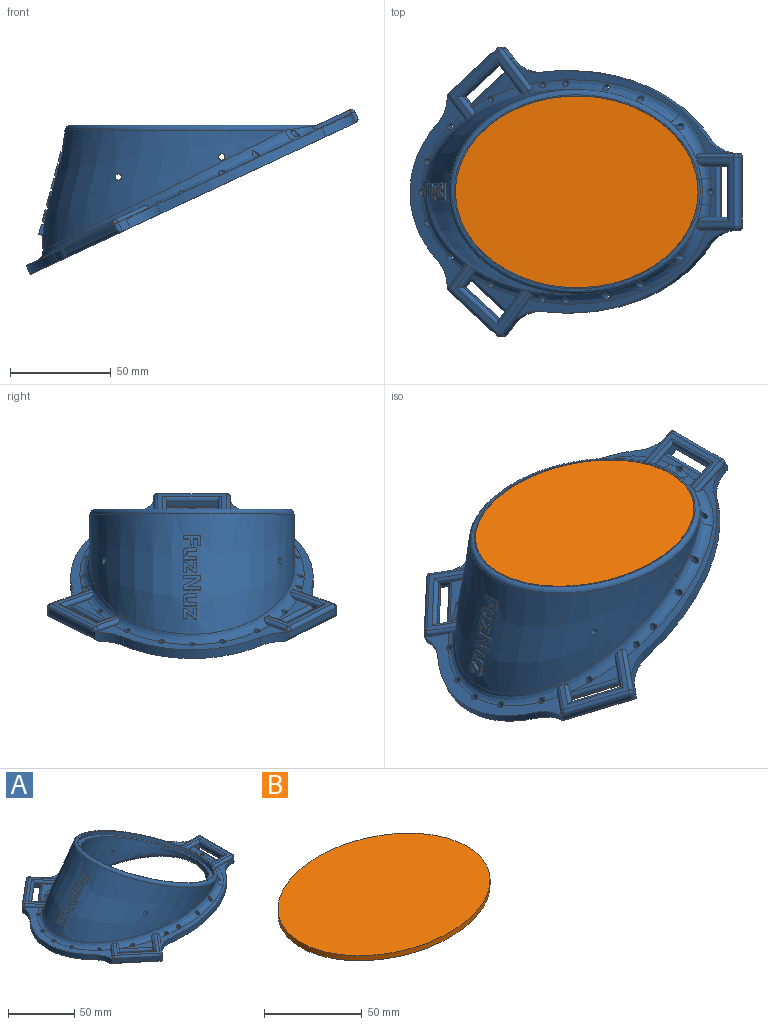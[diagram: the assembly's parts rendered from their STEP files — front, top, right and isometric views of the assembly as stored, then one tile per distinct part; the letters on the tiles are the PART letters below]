
ASSEMBLY  parts=2 mates=1
PART A: 209 faces, bbox 180.8x145.5x60.1 mm
  f0: bspline ~145.19x101.6mm, area 9514.1mm2, adj f10,f18,f19,f20,f21,f22,f125,f126
  f1: plane 24.98x16.69mm, normal (0,0,1), area 97.4mm2, adj f10,f36,f59,f60,f97
  f2: plane 13.2x11.08mm, normal (-0.77,-0.64,0), area 19.5mm2, adj f10,f11,f49,f87,f98,f100,f124
  f3: plane 178.75x142.51mm, normal (0,0,-1), area 5639.8mm2, adj f6,f8,f16,f24,f26,f27,f29,f30
  f4: bspline ~140.7x88.9mm, area 10555.1mm2, adj f18,f19,f20,f21,f67,f68
  f5: plane 25.41x3.72mm, normal (0,0,1), area 69.3mm2, adj f12,f13,f14,f27,f52,f53,f70
  f6: extruded ~90.53x33.28mm, area 480mm2, adj f3,f7,f85,f90
  f7: plane 122.83x47.16mm, normal (0,0,1), area 433.4mm2, adj f6,f10,f12,f35,f54,f62,f85,f90
  f8: extruded ~68.2x15.01mm, area 365mm2, adj f3,f9,f89,f92
  f9: plane 98.89x28.6mm, normal (0,0,1), area 617.6mm2, adj f8,f10,f24,f30,f31,f32,f37,f48
  f10: bspline ~145.09x111.78mm, area 2304.7mm2, adj f0,f1,f2,f7,f9,f11,f12,f14
  f11: plane 24.97x16.69mm, normal (0,0,1), area 97.4mm2, adj f2,f10,f33,f46,f98
  f12: bspline ~38.11x22.09mm, area 191.3mm2, adj f5,f7,f10,f13,f22,f28,f29,f51
  f13: bspline ~21.06x5.16mm, area 55.7mm2, adj f5,f12,f14,f23,f27
  f14: bspline ~37.9x21.75mm, area 191.3mm2, adj f5,f10,f13,f17,f22,f25,f26,f51
  f15: plane 110.97x96.55mm, normal (0.42,0,0.91), area 228.7mm2, adj f22,f23,f69
  f16: extruded ~90.53x33.28mm, area 480mm2, adj f3,f17,f86,f91
  f17: plane 122.83x47.16mm, normal (0,0,1), area 433.4mm2, adj f10,f14,f16,f34,f47,f55,f86,f91
  f18: cylinder r=1.59mm len=6.47mm, axis (0,-1,0), area 64.6mm2, adj f0,f4
  f19: cylinder r=1.59mm len=6.47mm, axis (0,-1,0), area 64.6mm2, adj f0,f4
  f20: cylinder r=1.59mm len=6.87mm, axis (0,-1,0), area 68.6mm2, adj f0,f4
  f21: cylinder r=1.59mm len=6.87mm, axis (0,-1,0), area 68.6mm2, adj f0,f4
  f22: bspline ~115.08x101.58mm, area 1264.8mm2, adj f0,f12,f14,f15,f23
  f23: bspline ~19.62x2.95mm, area 14.2mm2, adj f13,f15,f22
  f24: cylinder r=1.59mm len=4.78mm, axis (0,0,-1), area 47.6mm2, adj f3,f9,f10
  f25: cone r=0mm half-angle=59deg, axis (0,0,-1), area 1.7mm2, adj f14,f26
  f26: cylinder r=1.59mm len=9.53mm, axis (0,0,-1), area 74.5mm2, adj f3,f14,f25
  f27: cylinder r=1.59mm len=5.05mm, axis (0,0,-1), area 48.3mm2, adj f3,f5,f13
  f28: cone r=0mm half-angle=59deg, axis (0,0,-1), area 1.7mm2, adj f12,f29
  f29: cylinder r=1.59mm len=9.53mm, axis (0,0,-1), area 74.5mm2, adj f3,f12,f28
  f30: cylinder r=1.59mm len=4.78mm, axis (0,0,-1), area 47.6mm2, adj f3,f9,f10
  f31: cylinder r=1.59mm len=4.78mm, axis (0,0,-1), area 47.6mm2, adj f3,f9,f10
  f32: cylinder r=1.59mm len=5.31mm, axis (0,0,-1), area 49.2mm2, adj f3,f9,f10
  f33: cylinder r=1.59mm len=5.53mm, axis (0,0,-1), area 50.1mm2, adj f3,f10,f11
  f34: cylinder r=1.59mm len=5.89mm, axis (0,0,-1), area 51.7mm2, adj f3,f10,f17
  f35: cylinder r=1.59mm len=5.89mm, axis (0,0,-1), area 51.7mm2, adj f3,f7,f10
  f36: cylinder r=1.59mm len=5.53mm, axis (0,0,-1), area 50.1mm2, adj f1,f3,f10
  f37: cylinder r=1.59mm len=5.31mm, axis (0,0,-1), area 49.2mm2, adj f3,f9,f10
  f38: cylinder r=1.59mm len=5.11mm, axis (0,0,-1), area 51mm2, adj f3,f10
  f39: cylinder r=1.59mm len=5.61mm, axis (0,0,-1), area 56mm2, adj f3,f10
  f40: cylinder r=1.59mm len=8.91mm, axis (0,0,-1), area 64.6mm2, adj f3,f10
  f41: cylinder r=1.59mm len=8.91mm, axis (0,0,-1), area 64.6mm2, adj f3,f10
  f42: cylinder r=1.59mm len=5.61mm, axis (0,0,-1), area 56mm2, adj f3,f10
  f43: cylinder r=1.59mm len=5.11mm, axis (0,0,-1), area 51mm2, adj f3,f10
  f44: plane 43.13x33.71mm, normal (0,0,1), area 179.1mm2, adj f10,f45,f114,f117,f118,f122,f123,f124
  f45: plane 2.15x1.82mm, normal (0.64,-0.77,0), area 1.3mm2, adj f10,f44,f117
  f46: plane 6.87x5.77mm, normal (0.77,0.64,0), area 17mm2, adj f10,f11,f49,f87,f98,f101,f122
  f47: plane 19.16x16.08mm, normal (0.77,0.64,0), area 38.9mm2, adj f3,f10,f17,f91,f117,f121
  f48: plane 9.68x8.13mm, normal (-0.77,-0.64,0), area 3.7mm2, adj f9,f10,f114,f115
  f49: plane 19.46x16.33mm, normal (0.64,-0.77,0), area 80.6mm2, adj f2,f46,f99,f123
  f50: plane 27.73x23.27mm, normal (-0.64,0.77,0), area 114.3mm2, adj f9,f92,f115,f118,f120,f121
  f51: plane 34.3x20.36mm, normal (0,0,1), area 175.5mm2, adj f12,f14,f74,f76,f77,f82,f83,f84
  f52: plane 14.1x5.12mm, normal (0,-1,0), area 28.7mm2, adj f3,f5,f14,f56,f66,f70,f71,f73
  f53: plane 12.19x3.21mm, normal (0,1,0), area 18mm2, adj f5,f12,f56,f66,f70,f72,f84
  f54: plane 18.45x5.13mm, normal (0,-1,0), area 9.6mm2, adj f3,f7,f12,f76,f81,f85
  f55: plane 18.44x5.12mm, normal (0,1,0), area 9.6mm2, adj f3,f14,f17,f74,f78,f86
  f56: plane 25.4x3.18mm, normal (-1,0,0), area 80.6mm2, adj f52,f53,f71,f83
  f57: plane 34.29x3.18mm, normal (1,0,0), area 108.9mm2, adj f77,f78,f80,f81
  f58: plane 43.13x33.71mm, normal (0,0,1), area 179.1mm2, adj f10,f63,f104,f107,f108,f111,f112,f113
  f59: plane 13.2x11.09mm, normal (-0.77,0.64,0), area 19.5mm2, adj f1,f10,f64,f88,f94,f97,f111
  f60: plane 6.87x5.77mm, normal (0.77,-0.64,0), area 17mm2, adj f1,f10,f64,f88,f95,f97,f113
  f61: plane 9.68x8.13mm, normal (-0.77,0.64,0), area 3.7mm2, adj f9,f10,f107,f110
  f62: plane 19.16x16.08mm, normal (0.77,-0.64,0), area 38.9mm2, adj f3,f7,f10,f90,f104,f105
  f63: plane 2.15x1.82mm, normal (0.64,0.77,0), area 1.3mm2, adj f10,f58,f104
  f64: plane 19.46x16.33mm, normal (0.64,0.77,0), area 80.6mm2, adj f59,f60,f93,f112
  f65: plane 27.73x23.27mm, normal (-0.64,-0.77,0), area 114.3mm2, adj f9,f89,f103,f105,f108,f110
  f66: plane 25.4x0.97mm, normal (1,0,0), area 24.5mm2, adj f52,f53,f70,f73
  f67: bspline ~145.83x95.27mm, area 1856.2mm2, adj f3,f4
  f68: plane 109.35x95.25mm, normal (0.42,0,0.91), area 1021.6mm2, adj f4,f69
  f69: extruded ~110.69x95.25mm, area 1080.5mm2, adj f15,f68
  f70: cylinder r=1.91mm len=25.4mm, axis (0,1,0), area 76mm2, adj f5,f52,f53,f66
  f71: cylinder r=1.91mm len=27.31mm, axis (0,-1,0), area 78.9mm2, adj f3,f52,f56,f72
  f72: cylinder r=1.91mm len=8.59mm, axis (-1,0,0), area 20mm2, adj f3,f53,f71,f73
  f73: cylinder r=1.91mm len=27.31mm, axis (0,1,0), area 78.9mm2, adj f3,f52,f66,f72
  f74: cylinder r=1.91mm len=20.34mm, axis (1,0,0), area 58mm2, adj f14,f51,f55,f75
  f75: sphere r=1.91mm, area 3.6mm2, adj f74,f77,f78
  f76: cylinder r=1.91mm len=20.34mm, axis (-1,0,0), area 58mm2, adj f12,f51,f54,f79
  f77: cylinder r=1.91mm len=34.29mm, axis (0,-1,0), area 102.6mm2, adj f51,f57,f75,f79
  f78: cylinder r=1.91mm len=5.08mm, axis (0,0,-1), area 12.4mm2, adj f55,f57,f75,f80
  f79: sphere r=1.91mm, area 3.6mm2, adj f76,f77,f81
  f80: cylinder r=1.91mm len=38.1mm, axis (0,1,0), area 108.3mm2, adj f3,f57,f78,f81
  f81: cylinder r=1.91mm len=5.08mm, axis (0,0,-1), area 12.4mm2, adj f54,f57,f79,f80
  f82: cylinder r=1.91mm len=17.05mm, axis (-1,0,0), area 43.7mm2, adj f14,f51,f52,f83
  f83: cylinder r=1.91mm len=29.21mm, axis (0,1,0), area 81.7mm2, adj f51,f56,f82,f84
  f84: cylinder r=1.91mm len=17.05mm, axis (1,0,0), area 43.7mm2, adj f12,f51,f53,f83
  f85: cylinder r=19.05mm len=15.51mm, axis (0,0,-1), area 86.6mm2, adj f3,f6,f7,f54
  f86: cylinder r=19.05mm len=15.51mm, axis (0,0,-1), area 86.6mm2, adj f3,f16,f17,f55
  f87: plane 19.46x16.33mm, normal (-0.64,0.77,0), area 24.5mm2, adj f2,f46,f98,f102
  f88: plane 19.46x16.33mm, normal (-0.64,-0.77,0), area 24.5mm2, adj f59,f60,f96,f97
  f89: cylinder r=19.05mm len=14.12mm, axis (0,0,-1), area 71.8mm2, adj f3,f8,f9,f65,f103
  f90: cylinder r=19.05mm len=16.78mm, axis (0,0,-1), area 89.9mm2, adj f3,f6,f7,f62
  f91: cylinder r=19.05mm len=16.78mm, axis (0,0,-1), area 89.9mm2, adj f3,f16,f17,f47
  f92: cylinder r=19.05mm len=14.12mm, axis (0,0,-1), area 71.8mm2, adj f3,f8,f9,f50,f120
  f93: cylinder r=1.91mm len=23.6mm, axis (-0.77,0.64,0), area 81.7mm2, adj f3,f64,f94,f95
  f94: cylinder r=1.91mm len=7.8mm, axis (-0.64,-0.77,0), area 20mm2, adj f3,f59,f93,f96
  f95: cylinder r=1.91mm len=7.8mm, axis (0.64,0.77,0), area 20mm2, adj f3,f60,f93,f96
  f96: cylinder r=1.91mm len=23.6mm, axis (0.77,-0.64,0), area 81.7mm2, adj f3,f88,f94,f95
  f97: cylinder r=1.91mm len=20.68mm, axis (-0.77,0.64,0), area 76mm2, adj f1,f59,f60,f88
  f98: cylinder r=1.91mm len=20.68mm, axis (-0.77,-0.64,0), area 76mm2, adj f2,f11,f46,f87
  f99: cylinder r=1.91mm len=23.6mm, axis (0.77,0.64,0), area 81.7mm2, adj f3,f49,f100,f101
  f100: cylinder r=1.91mm len=7.8mm, axis (0.64,-0.77,0), area 20mm2, adj f2,f3,f99,f102
  f101: cylinder r=1.91mm len=7.8mm, axis (-0.64,0.77,0), area 20mm2, adj f3,f46,f99,f102
  f102: cylinder r=1.91mm len=23.6mm, axis (-0.77,-0.64,0), area 81.7mm2, adj f3,f87,f100,f101
  f103: cylinder r=1.91mm len=31.69mm, axis (0.77,-0.64,0), area 113.7mm2, adj f3,f65,f89,f105
  f104: cylinder r=1.91mm len=21.32mm, axis (-0.64,-0.77,0), area 78.1mm2, adj f10,f58,f62,f63,f106
  f105: cylinder r=1.91mm len=5.08mm, axis (0,0,1), area 12.4mm2, adj f62,f65,f103,f106
  f106: sphere r=1.91mm, area 5.7mm2, adj f104,f105,f108
  f107: cylinder r=1.91mm len=12.89mm, axis (0.64,0.77,0), area 41.6mm2, adj f10,f58,f61,f109
  f108: cylinder r=1.91mm len=27.49mm, axis (-0.77,0.64,0), area 102.6mm2, adj f58,f65,f106,f109
  f109: sphere r=1.91mm, area 8.1mm2, adj f107,f108,f110
  f110: cylinder r=1.91mm len=2.68mm, axis (0,0,-1), area 0.9mm2, adj f9,f61,f65,f109
  f111: cylinder r=1.91mm len=18.68mm, axis (0.64,0.77,0), area 59.8mm2, adj f10,f58,f59,f112
  f112: cylinder r=1.91mm len=23.6mm, axis (0.77,-0.64,0), area 81.7mm2, adj f58,f64,f111,f113
  f113: cylinder r=1.91mm len=11.19mm, axis (-0.64,-0.77,0), area 32.8mm2, adj f10,f58,f60,f112
  f114: cylinder r=1.91mm len=12.89mm, axis (-0.64,0.77,0), area 41.6mm2, adj f10,f44,f48,f116
  f115: cylinder r=1.91mm len=2.68mm, axis (0,0,-1), area 0.9mm2, adj f9,f48,f50,f116
  f116: sphere r=1.91mm, area 5.7mm2, adj f114,f115,f118
  f117: cylinder r=1.91mm len=21.32mm, axis (0.64,-0.77,0), area 78.1mm2, adj f10,f44,f45,f47,f119
  f118: cylinder r=1.91mm len=27.49mm, axis (0.77,0.64,0), area 102.6mm2, adj f44,f50,f116,f119
  f119: sphere r=1.91mm, area 7.8mm2, adj f117,f118,f121
  f120: cylinder r=1.91mm len=31.69mm, axis (-0.77,-0.64,0), area 113.7mm2, adj f3,f50,f92,f121
  f121: cylinder r=1.91mm len=5.08mm, axis (0,0,1), area 12.4mm2, adj f47,f50,f119,f120
  f122: cylinder r=1.91mm len=11.19mm, axis (0.64,-0.77,0), area 32.8mm2, adj f10,f44,f46,f123
  f123: cylinder r=1.91mm len=23.6mm, axis (-0.77,-0.64,0), area 81.7mm2, adj f44,f49,f122,f124
  f124: cylinder r=1.91mm len=18.68mm, axis (-0.64,0.77,0), area 59.8mm2, adj f2,f10,f44,f123
  f125: plane 1.99x1.81mm, normal (0,1,0), area 1.6mm2, adj f0,f126,f132,f134
  f126: plane 8.61x0.65mm, normal (0.64,0,0.77), area 6mm2, adj f0,f125,f127,f132
  f127: plane 4.49x3.84mm, normal (0,-1,0), area 4.8mm2, adj f0,f126,f128,f132
  f128: plane 1.5x0.82mm, normal (-0.64,0,-0.77), area 1.5mm2, adj f0,f127,f129,f132
  f129: plane 3.02x2.66mm, normal (0,1,0), area 2.8mm2, adj f0,f128,f130,f132
  f130: plane 2.23x0.64mm, normal (-0.64,0,-0.77), area 1.7mm2, adj f0,f129,f131,f132
  f131: plane 2.79x2.45mm, normal (0,-1,0), area 2.3mm2, adj f0,f130,f132,f133
  f132: plane 8.61x3.78mm, normal (-0.77,0,0.64), area 24.5mm2, adj f125,f126,f127,f128,f129,f130,f131,f133
  f133: plane 1.5x0.66mm, normal (-0.64,0,-0.77), area 1.3mm2, adj f0,f131,f132,f135
  f134: plane 3.43x0.76mm, normal (-0.64,0,-0.77), area 2.8mm2, adj f0,f125,f132,f135
  f135: plane 2.79x2.45mm, normal (0,1,0), area 2.3mm2, adj f0,f132,f133,f134
  f136: plane 0.97x0.92mm, normal (0.62,0.28,0.74), area 1mm2, adj f0,f137,f150,f152
  f137: plane 0.88x0.76mm, normal (0,1,0), area 0.1mm2, adj f0,f136,f138,f150
  f138: extruded ~1.39x1.35mm, area 1.2mm2, adj f0,f137,f139,f150
  f139: extruded ~1.66x1.66mm, area 1.4mm2, adj f0,f138,f140,f150
  f140: extruded ~2.08x2mm, area 2.1mm2, adj f0,f139,f141,f150
  f141: extruded ~1.79x1.2mm, area 1.9mm2, adj f0,f140,f142,f150
  f142: plane 4.29x0.72mm, normal (0.64,0,0.77), area 3.9mm2, adj f0,f141,f143,f150
  f143: plane 2x1.88mm, normal (0,-1,0), area 1.7mm2, adj f0,f142,f144,f150
  f144: plane 3.88x0.78mm, normal (-0.64,0,-0.77), area 3.6mm2, adj f0,f143,f145,f150
  f145: extruded ~1.07x0.93mm, area 1.1mm2, adj f0,f144,f146,f150
  f146: extruded ~1.3x1.28mm, area 0.9mm2, adj f0,f145,f147,f150
  f147: extruded ~1.49x1.49mm, area 1.3mm2, adj f0,f146,f148,f150
  f148: extruded ~1.67x0.98mm, area 1.7mm2, adj f0,f147,f149,f150
  f149: plane 3.12x0.78mm, normal (0.64,0,0.77), area 2.9mm2, adj f0,f148,f150,f151
  f150: plane 6.7x4.65mm, normal (-0.77,0,0.64), area 26.4mm2, adj f136,f137,f138,f139,f140,f141,f142,f143
  f151: plane 2x1.91mm, normal (0,-1,0), area 1.8mm2, adj f0,f149,f150,f153
  f152: plane 1.79x1.76mm, normal (0,1,0), area 1.6mm2, adj f0,f136,f150,f153
  f153: plane 6.58x0.87mm, normal (-0.64,0,-0.77), area 6.4mm2, adj f0,f150,f151,f152
  f154: plane 4.68x4.21mm, normal (0,1,0), area 5.7mm2, adj f0,f155,f161,f163
  f155: plane 1.06x0.87mm, normal (0.64,0,0.77), area 1.1mm2, adj f0,f154,f156,f161
  f156: plane 4.16x2.91mm, normal (0.52,-0.59,0.62), area 4.8mm2, adj f0,f155,f157,f161
  f157: plane 2.77x2.55mm, normal (0,1,0), area 2.6mm2, adj f0,f156,f158,f161
  f158: plane 1.38x0.75mm, normal (0.64,0,0.77), area 1.3mm2, adj f0,f157,f159,f161
  f159: plane 4.36x3.9mm, normal (0,-1,0), area 4.6mm2, adj f0,f158,f160,f161
  f160: plane 1.17x0.71mm, normal (-0.64,0,-0.77), area 1mm2, adj f0,f159,f161,f162
  f161: plane 6.58x3.98mm, normal (-0.77,0,0.64), area 21.1mm2, adj f154,f155,f156,f157,f158,f159,f160,f162
  f162: plane 4.05x2.84mm, normal (-0.52,0.59,-0.62), area 4.5mm2, adj f0,f160,f161,f164
  f163: plane 1.38x0.83mm, normal (-0.64,0,-0.77), area 1.4mm2, adj f0,f154,f161,f164
  f164: plane 2.98x2.74mm, normal (0,-1,0), area 3mm2, adj f0,f161,f162,f163
  f165: plane 2.48x2.31mm, normal (0,1,0), area 2.5mm2, adj f0,f166,f176,f178
  f166: plane 6.51x3.55mm, normal (0.56,0.5,0.66), area 6.7mm2, adj f0,f165,f167,f176
  f167: plane 0.72x0.61mm, normal (0,1,0), area 0mm2, adj f0,f166,f168,f176
  f168: extruded ~2.46x0.76mm, area 2.1mm2, adj f0,f167,f169,f176
  f169: plane 4.05x0.81mm, normal (-0.64,0,-0.77), area 3.7mm2, adj f0,f168,f170,f176
  f170: plane 1.93x1.87mm, normal (0,1,0), area 1.7mm2, adj f0,f169,f171,f176
  f171: plane 8.61x0.82mm, normal (0.64,0,0.77), area 7.9mm2, adj f0,f170,f172,f176
  f172: plane 2.44x2.3mm, normal (0,-1,0), area 2.4mm2, adj f0,f171,f173,f176
  f173: plane 6.45x3.44mm, normal (-0.56,-0.5,-0.66), area 6.6mm2, adj f0,f172,f174,f176
  f174: plane 0.71x0.61mm, normal (0,-1,0), area 0mm2, adj f0,f173,f175,f176
  f175: extruded ~2.37x0.75mm, area 2.1mm2, adj f0,f174,f176,f177
  f176: plane 8.61x5.85mm, normal (-0.77,0,0.64), area 42mm2, adj f165,f166,f167,f168,f169,f170,f171,f172
  f177: plane 4.07x0.81mm, normal (0.64,0,0.77), area 3.7mm2, adj f0,f175,f176,f179
  f178: plane 8.61x0.84mm, normal (-0.64,0,-0.77), area 8.1mm2, adj f0,f165,f176,f179
  f179: plane 1.96x1.87mm, normal (0,-1,0), area 1.8mm2, adj f0,f176,f177,f178
  f180: plane 1.14x1.08mm, normal (0.62,0.28,0.74), area 1.2mm2, adj f0,f181,f194,f196
  f181: plane 1.04x0.9mm, normal (0,1,0), area 0.1mm2, adj f0,f180,f182,f194
  f182: extruded ~1.51x1.46mm, area 1.4mm2, adj f0,f181,f183,f194
  f183: extruded ~1.76x1.75mm, area 1.6mm2, adj f0,f182,f184,f194
  f184: extruded ~2.14x2.08mm, area 2.3mm2, adj f0,f183,f185,f194
  f185: extruded ~1.79x1.23mm, area 2mm2, adj f0,f184,f186,f194
  f186: plane 4.29x0.75mm, normal (0.64,0,0.77), area 4mm2, adj f0,f185,f187,f194
  f187: plane 2.05x1.91mm, normal (0,-1,0), area 1.8mm2, adj f0,f186,f188,f194
  f188: plane 3.85x0.8mm, normal (-0.64,0,-0.77), area 3.8mm2, adj f0,f187,f189,f194
  f189: extruded ~1.07x0.99mm, area 1.2mm2, adj f0,f188,f190,f194
  f190: extruded ~1.4x1.35mm, area 1mm2, adj f0,f189,f191,f194
  f191: extruded ~1.6x1.59mm, area 1.5mm2, adj f0,f190,f192,f194
  f192: extruded ~1.67x1.12mm, area 2mm2, adj f0,f191,f193,f194
  f193: plane 3.13x0.94mm, normal (0.64,0,0.77), area 3.5mm2, adj f0,f192,f194,f195
  f194: plane 6.7x4.65mm, normal (-0.77,0,0.64), area 26.4mm2, adj f180,f181,f182,f183,f184,f185,f186,f187
  f195: plane 2.23x2.07mm, normal (0,-1,0), area 2.2mm2, adj f0,f193,f194,f197
  f196: plane 2.02x1.95mm, normal (0,1,0), area 2mm2, adj f0,f180,f194,f197
  f197: plane 6.58x1.15mm, normal (-0.64,0,-0.77), area 8.7mm2, adj f0,f194,f195,f196
  f198: plane 5.51x4.58mm, normal (0,1,0), area 10.2mm2, adj f0,f199,f205,f207
  f199: plane 1.24x1.07mm, normal (0.64,0,0.77), area 1.7mm2, adj f0,f198,f200,f205
  f200: plane 4.15x3.48mm, normal (0.52,-0.59,0.62), area 8.2mm2, adj f0,f199,f201,f205
  f201: plane 3.35x2.94mm, normal (0,1,0), area 4.5mm2, adj f0,f200,f202,f205
  f202: plane 1.38x1.13mm, normal (0.64,0,0.77), area 2mm2, adj f0,f201,f203,f205
  f203: plane 5.16x4.28mm, normal (0,-1,0), area 8.8mm2, adj f0,f202,f204,f205
  f204: plane 1.67x1.4mm, normal (-0.64,0,-0.77), area 2.5mm2, adj f0,f203,f205,f206
  f205: plane 6.58x3.98mm, normal (-0.77,0,0.64), area 21.1mm2, adj f198,f199,f200,f201,f202,f203,f204,f206
  f206: plane 4.05x3.64mm, normal (-0.52,0.59,-0.62), area 9.4mm2, adj f0,f204,f205,f208
  f207: plane 1.83x1.53mm, normal (-0.64,0,-0.77), area 3.2mm2, adj f0,f198,f205,f208
  f208: plane 3.82x3.33mm, normal (0,-1,0), area 6.1mm2, adj f0,f205,f206,f207
PART B: 3 faces, bbox 120.7x95.3x3.2 mm
  f0: extruded ~120.65x95.25mm, area 1080.5mm2, adj f1,f2
  f1: plane 120.65x95.25mm, normal (0,0,1), area 9025.7mm2, adj f0
  f2: plane 120.65x95.25mm, normal (0,0,-1), area 9025.7mm2, adj f0
PLACE A rot(axis=(0,-1,0),25deg) t=(5.9,59.75,45.18)mm
PLACE B t=(9.16,59.75,80.11)mm
MATE fastened A.f68 <-> B.f2  axis (0,0,1) through (9.16,59.75,80.11)mm
